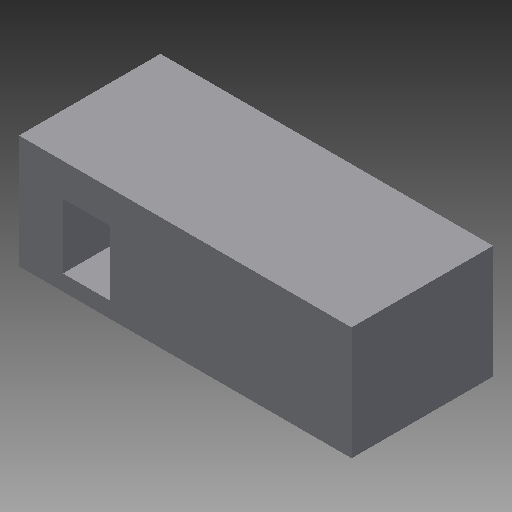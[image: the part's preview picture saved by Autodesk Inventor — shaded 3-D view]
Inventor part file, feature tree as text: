
AUTODESK INVENTOR PART (.ipt)
format: ipt  version: 2017 (Build 210142000, 142)  size: 123,904 bytes
history: native  units: mm
features: extrude x4, sketch x2, plane x1
ambient origin geometry x8: Origin, YZ Plane, XZ Plane, XY Plane, X Axis, Y Axis, Z Axis, Center Point
bodies: Solid1 (feature_tree)
feature tree (7):
  extrude  "Extrusion1"  Depth=6.0mm
  plane  "Work Plane10"
  extrude  "Extrusion25"  Depth=1.0mm TaperAngle=0.0deg
  extrude  "Extrusion26"  Depth=1.0mm TaperAngle=0.0deg
  extrude  "Extrusion27"  Depth=6.0mm TaperAngle=0.0deg
  sketch  "Sketch20"  dims[d1=12.0mm d2=0.0mm d4=6.0mm]
  sketch  "Sketch21"  dims[d108=5.3mm d110=1.0mm d111=0.0mm d112=1.0mm d113=0.0mm d114=6.0mm d115=0.0mm]
